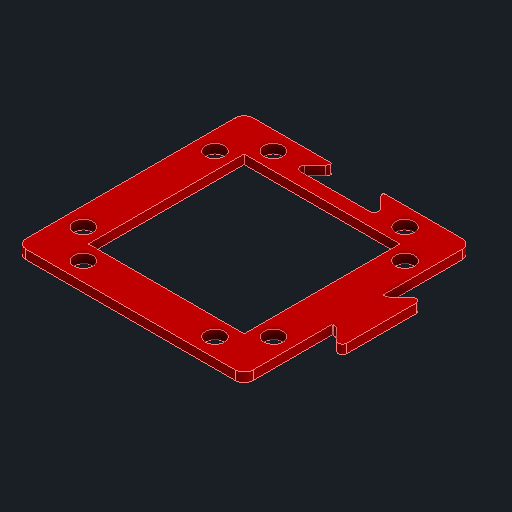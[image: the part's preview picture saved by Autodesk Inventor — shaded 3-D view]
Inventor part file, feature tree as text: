
AUTODESK INVENTOR PART (.ipt)
format: ipt  version: 2023.4 (Build 274418000, 418)  size: 378,880 bytes
history: native  units: mm
features: reference x9, extrude x3, other x3, sketch x2, fillet x1, projected_geometry x1
ambient origin geometry x8: Origin, YZ Plane, XZ Plane, XY Plane, X Axis, Y Axis, Z Axis, Center Point
bodies: Solid1 (feature_tree)
feature tree (19):
  extrude  "Extrusion1"  Depth=2.0mm TaperAngle=0.0deg
  sketch  "Sketch2"  dims[d16=10.0mm d17=0.0mm d18=0.25mm d19=20.0mm d20=10.0mm d21=45.0deg d22=1.0mm d23=1.5mm d24=1.0mm d25=0.075mm d28=15.171573mm d29=2.87868mm d30=2.87868mm d31=20.0mm d32=10.0mm d33=45.0deg d34=1.0mm d35=1.5mm d36=1.0mm d37=0.075mm d38=15.171573mm d39=2.87868mm d40=2.87868mm d41=0.25mm d42=0.0mm d43=40.0mm d45=360.0deg]
  extrude  "Extrusion2"  Depth=0.25mm
  extrude  "Extrusion3"  Depth=0.25mm
  fillet  "Fillet1"  Radius=2.87868mm
  sketch  "Sketch1"  dims[d0=2.0mm d1=0.0mm d14=2.0mm d15=0.0mm]
  reference  "Reference1"
  reference  "Reference2"
  reference  "Reference3"
  reference  "Reference4"
  reference  "Reference5"
  reference  "Reference6"
  reference  "Reference7"
  reference  "Reference8"
  reference  "Reference9"
  projected_geometry  "Projected Loop2"
  other  "<path>\Projects\Project Protocube\Protocube\CAD, STL, OBJ Files\1 CAD\Cube 1x1 V5.iam"
  other  "Cube 1x1 V5.iam"
  other  "Cube 1x1 Top V5:1"
note: 1 file-system path scrubbed to <path> (originals preserved in map.json)
